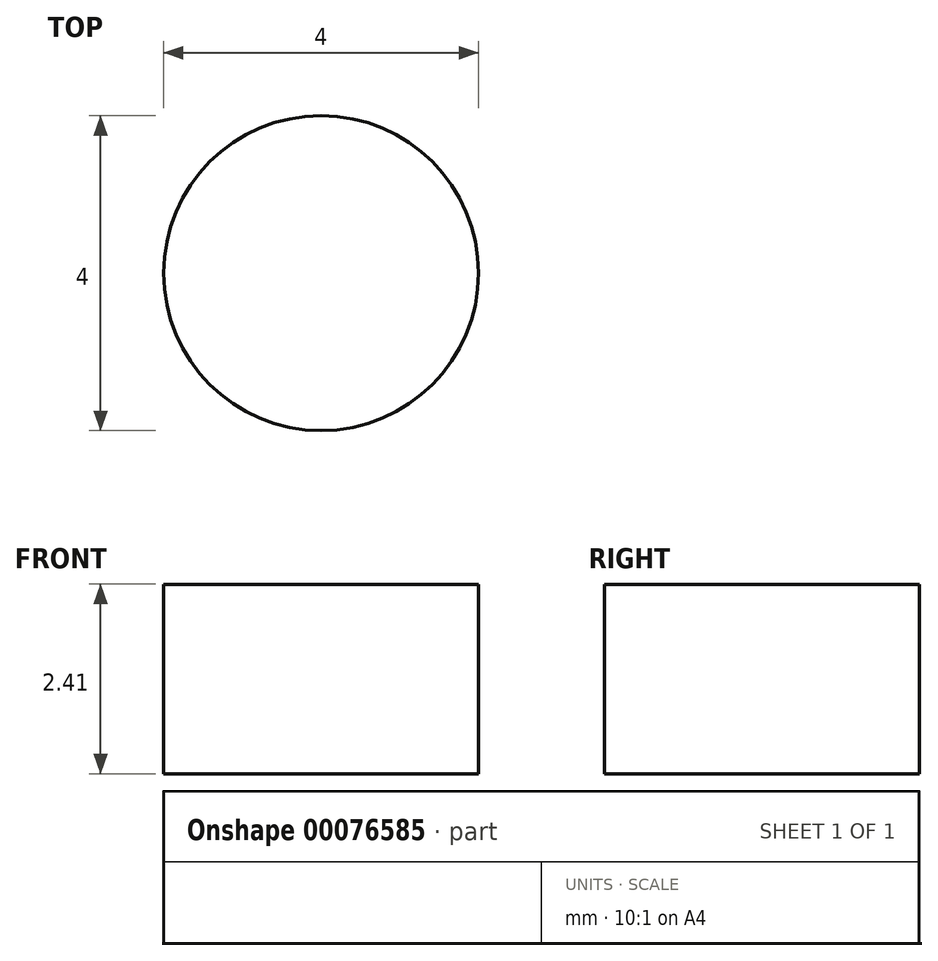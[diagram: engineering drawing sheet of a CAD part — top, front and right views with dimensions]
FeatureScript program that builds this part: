
annotation { "Feature Type Name" : "Feature", "Feature Type Description" : "" }
export const myFeature = defineFeature(function(context is Context, id is Id, definition is map)
    precondition{}
    {
        {
            var Q0;
            Q0=qCreatedBy(makeId("Top.planeOp"),FACE);
            var sketch = newSketch(context, id + "F0", { "sketchPlane" : qUnion([Q0])});
            skCircle(sketch, "E0", {"center": v(0, 0) * mm, "radius": 2 * mm});
            skSolve(sketch);
        }
        {
            var Q0;
            Q0 = qSketchRegion(id + "F0", true);
            extrude(context, id + "F1", {"entities" : qUnion([Q0]), "depth" : ((6 + 9 / 16) - (4 + 3 / 16) + 1 / 32) * mm});
        }
    });
